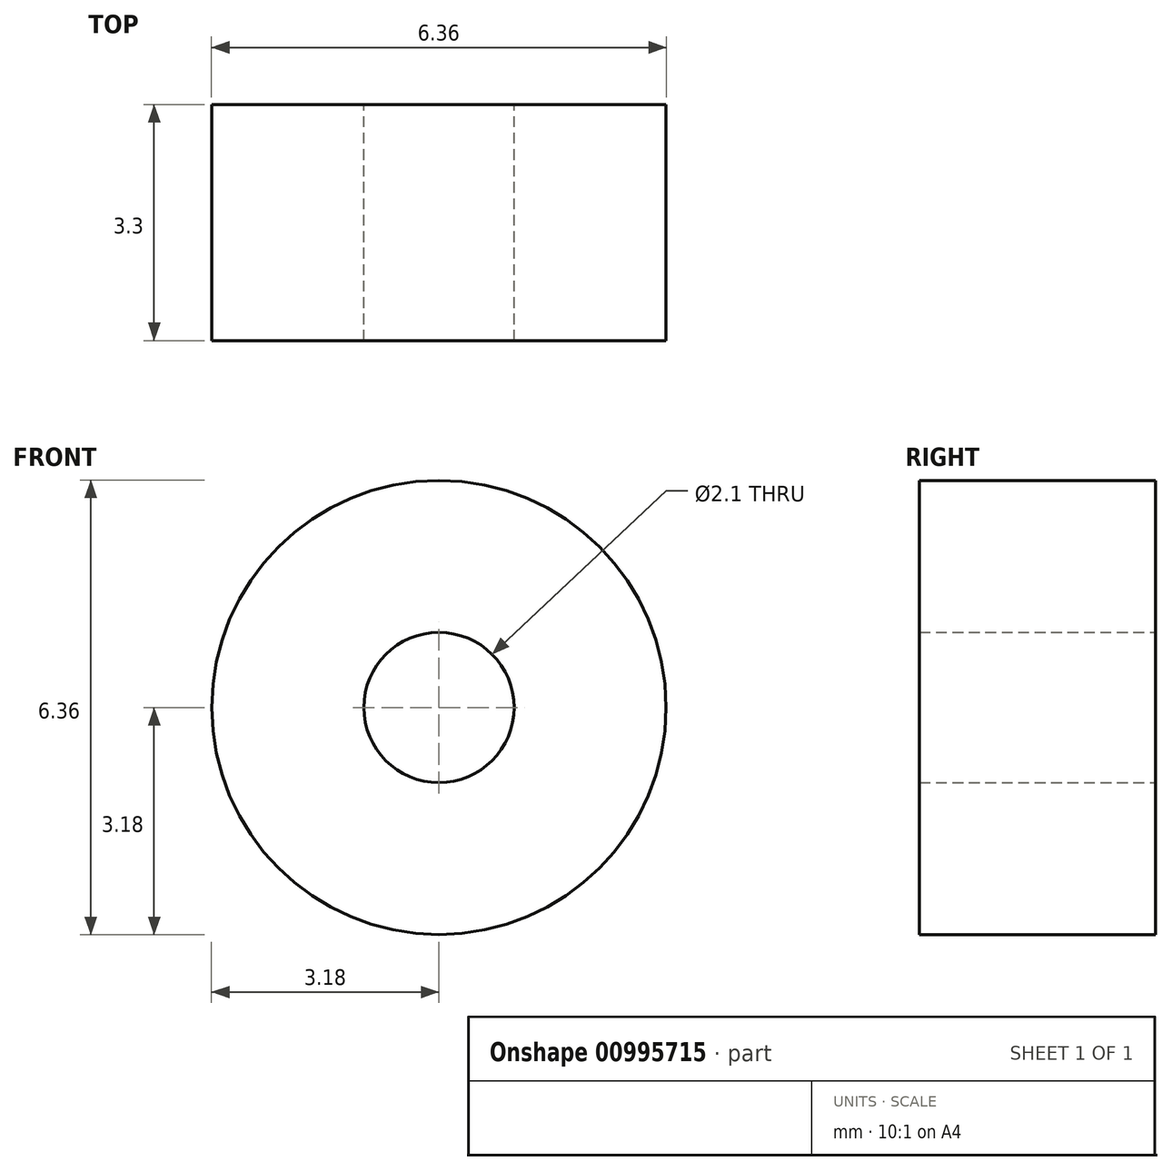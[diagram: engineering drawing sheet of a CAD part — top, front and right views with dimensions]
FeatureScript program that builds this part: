
annotation { "Feature Type Name" : "Feature", "Feature Type Description" : "" }
export const myFeature = defineFeature(function(context is Context, id is Id, definition is map)
    precondition{}
    {
        {
            var Q0;
            Q0=qCreatedBy(makeId("Front.planeOp"),FACE);
            var sketch = newSketch(context, id + "F0", { "sketchPlane" : qUnion([Q0])});
            skCircle(sketch, "E0", {"center": v(0, 0) * mm, "radius": 1.05 * mm});
            skCircle(sketch, "E1", {"center": v(0, 0) * mm, "radius": 3.18 * mm});
            skSolve(sketch);
        }
        {
            var Q0;
            Q0 = qSketchRegion(id + "F0", true);
            extrude(context, id + "F1", {"entities" : qUnion([Q0]), "depth" : 3.3 * mm, "offsetDistance" : 25.4 * mm});
        }
    });
